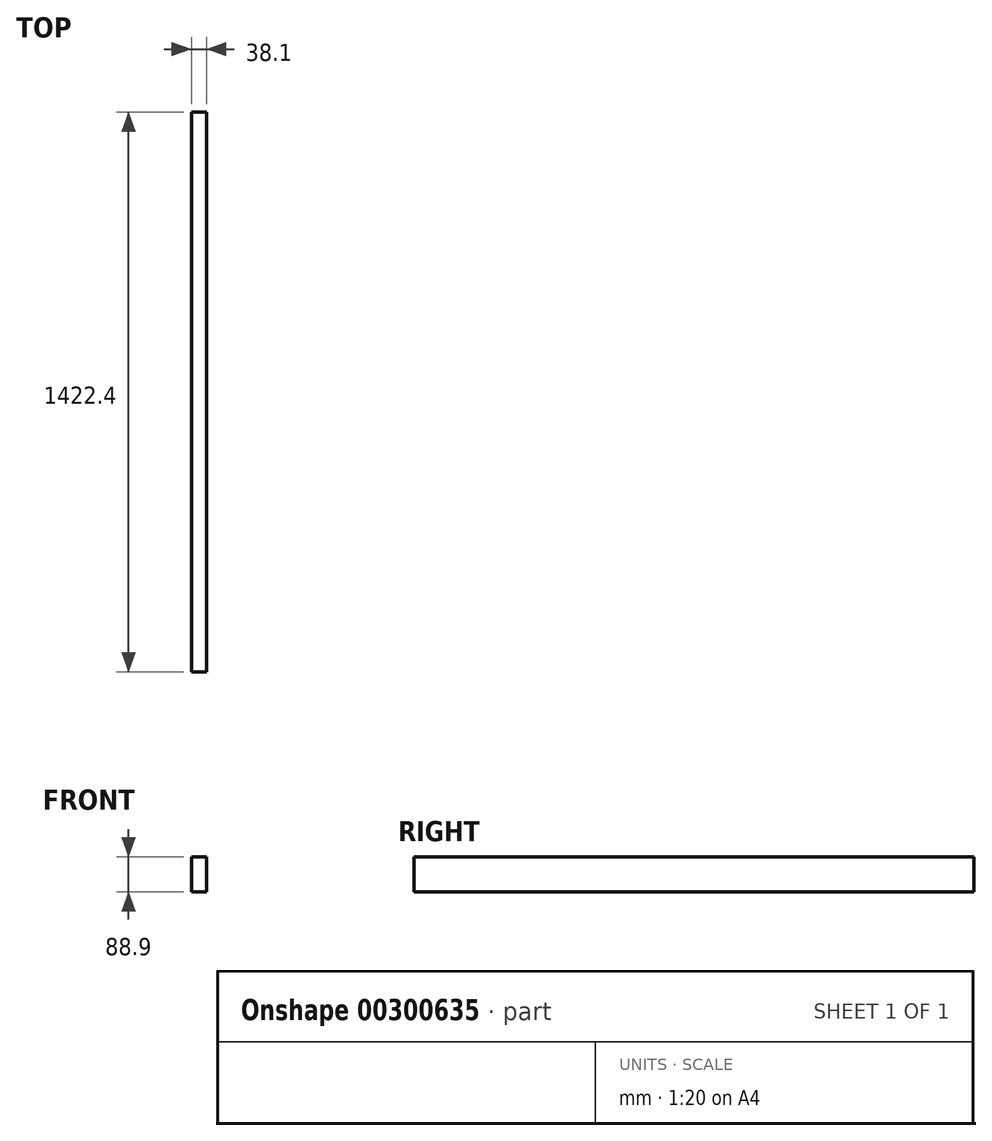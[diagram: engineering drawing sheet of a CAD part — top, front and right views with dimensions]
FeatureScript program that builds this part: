
annotation { "Feature Type Name" : "Feature", "Feature Type Description" : "" }
export const myFeature = defineFeature(function(context is Context, id is Id, definition is map)
    precondition{}
    {
        {
            var Q0;
            Q0=qCreatedBy(makeId("Front.planeOp"),FACE);
            var sketch = newSketch(context, id + "F0", { "sketchPlane" : qUnion([Q0])});
            skLineSegment(sketch, "E0.bottom", {"start": v(19.05, 44.45) * mm, "end": v(-19.05, 44.45) * mm});
            skLineSegment(sketch, "E0.top", {"start": v(19.05, -44.45) * mm, "end": v(-19.05, -44.45) * mm});
            skLineSegment(sketch, "E0.left", {"start": v(19.05, 44.45) * mm, "end": v(19.05, -44.45) * mm});
            skLineSegment(sketch, "E0.right", {"start": v(-19.05, 44.45) * mm, "end": v(-19.05, -44.45) * mm});
            skPoint(sketch, "E0.middle", {"position": v(0, 0) * mm});
            skSolve(sketch);
        }
        {
            var Q0;
            Q0=qSketchRegion(id+"F0",true);
            extrude(context, id + "F1", {"entities" : qUnion([Q0]), "oppositeDirection" : true, "depth" : 1422.4 * mm});
        }
    });
